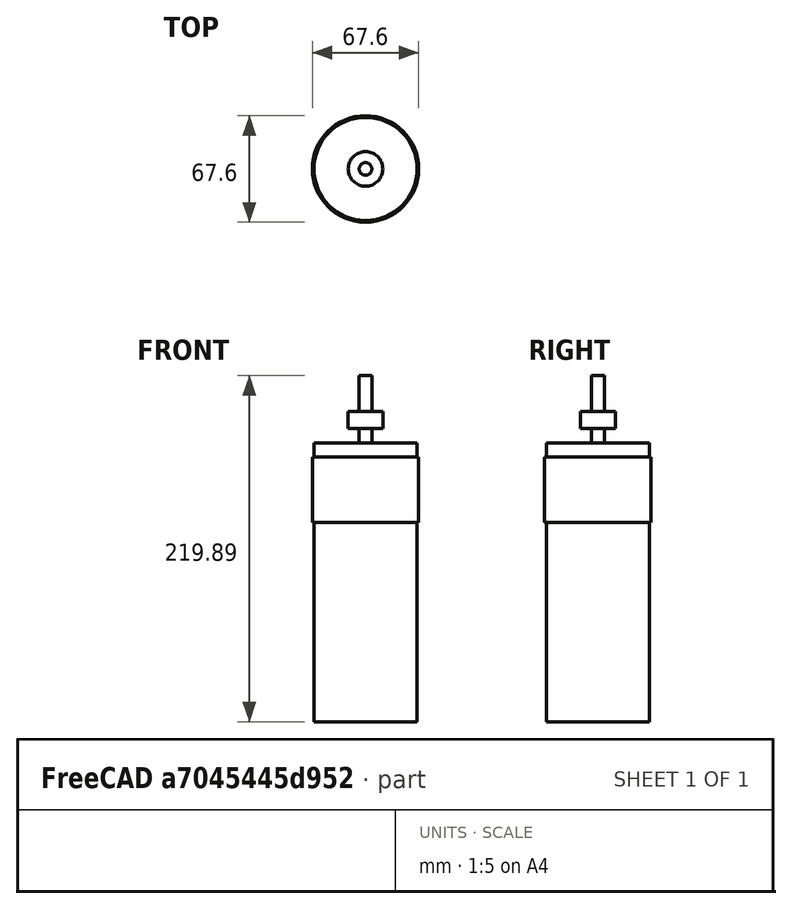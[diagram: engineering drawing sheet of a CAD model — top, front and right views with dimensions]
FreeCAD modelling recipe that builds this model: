
FCSTD DOCUMENT  (FreeCAD 1.0RUnknown)
Label: castle-router
License: All rights reserved
LicenseURL: https://en.wikipedia.org/wiki/All_rights_reserved
objects: Sketcher::SketchObject×1, PartDesign::Revolution×1, PartDesign::Body×1
note: 6 computed .brp shape members not serialized (recipe doc carries the construction recipe); baked Part::Feature solids carry a one-line shape summary decoded from their .brp

FEATURE [Sketcher::SketchObject] Sketch
  ArcFitTolerance = 1e-06
  AttachmentSupport = -> [XZ_Plane]
  FullyConstrained = true
  MakeInternals = false
  MapMode = 5
  Placement = pos=(0,0,0) rot=(1,0,0;1.5708rad)
  sketch-geometry (14):
    g0: LineSegment StartX=-32.75 StartY=176.98 StartZ=0 EndX=-32.75 EndY=168.13 EndZ=0
    g1: LineSegment StartX=-32.75 StartY=0 StartZ=0 EndX=0 EndY=0 EndZ=0
    g2: LineSegment StartX=-33.8 StartY=168.13 StartZ=0 EndX=-33.8 EndY=126.73 EndZ=0
    g3: LineSegment StartX=-33.8 StartY=126.73 StartZ=0 EndX=-32.75 EndY=126.73 EndZ=0
    g4: LineSegment StartX=-4 StartY=219.89 StartZ=0 EndX=-4 EndY=197.2 EndZ=0
    g5: LineSegment StartX=0 StartY=219.89 StartZ=0 EndX=-4 EndY=219.89 EndZ=0
    g6: LineSegment StartX=-11 StartY=197.2 StartZ=0 EndX=-11 EndY=186.2 EndZ=0
    g7: LineSegment StartX=-11 StartY=186.2 StartZ=0 EndX=-4 EndY=186.2 EndZ=0
    g8: LineSegment StartX=-32.75 StartY=168.13 StartZ=0 EndX=-33.8 EndY=168.13 EndZ=0
    g9: LineSegment StartX=-32.75 StartY=126.73 StartZ=0 EndX=-32.75 EndY=0 EndZ=0
    g10: LineSegment StartX=-4 StartY=186.2 StartZ=0 EndX=-4 EndY=176.98 EndZ=0
    g11: LineSegment StartX=-4 StartY=197.2 StartZ=0 EndX=-11 EndY=197.2 EndZ=0
    g12: LineSegment StartX=-4 StartY=176.98 StartZ=0 EndX=-32.75 EndY=176.98 EndZ=0
    g13: LineSegment StartX=0 StartY=219.89 StartZ=0 EndX=0 EndY=0 EndZ=0
  constraints (43):
    c: Coincident(g9,g1)
    c: Coincident(g12,g0)
    c: Vertical(g0)
    c: Horizontal(g1)
    c: Distance(g1,g12) = 176.98
    c: Coincident(g2,g3)
    c: Coincident(g8,g2)
    c: Vertical(g2)
    c: Horizontal(g3)
    c: Coincident(g5,g4)
    c: Vertical(g4)
    c: Horizontal(g5)
    c: Coincident(g6,g7)
    c: Coincident(g11,g6)
    c: Vertical(g6)
    c: Horizontal(g7)
    c: Coincident(g9,g3)
    c: DistanceY(g2,g2) = 41.4
    c: Distance(g0,g0) = 8.85
    c: DistanceX(g5,g5) = 4
    c: PointOnObject(g4,g11)
    c: PointOnObject(g11,g4)
    c: DistanceY(g4,g4) = 22.69
    c: Coincident(g7,g10)
    c: Coincident(g8,g0)
    c: Coincident(g12,g10)
    c: DistanceX(g1,g1) = 32.75
    c: DistanceY(g6,g6) = 11
    c: Distance(g10,g10) = 9.22
    c: Distance(g7,g-2) = 4
    c: Distance(g6,g-2) = 11
    c: Distance(g2,g-2) = 33.8
    c: Distance(g0,g-2) = 32.75
    c: Vertical(g9)
    c: Vertical(g10)
    c: Horizontal(g8)
    c: Horizontal(g12)
    c: Horizontal(g11)
    c: PointOnObject(g1,g-1)
    c: PointOnObject(g5,g-2)
    c: Equal(g3,g8)
    c: Coincident(g13,g5)
    c: Coincident(g13,g1)
FEATURE [PartDesign::Revolution] Revolution  label="RouterBody"
  Angle = 360
  Angle2 = 60
  Axis = (0,2e-16,1)
  Base = (0,0,0)
  Placement = pos=(0,0,0) rot=(1,0,0;1.5708rad)
  Profile = -> Sketch
  ReferenceAxis = -> Sketch [V_Axis]
  Refine = true
  Suppressed = false
  Type = 0
FEATURE [PartDesign::Body] Body  label="Router"
  AllowCompound = false
  Group = -> [Sketch,Revolution]
  Origin = -> Origin
  Tip = -> Revolution
